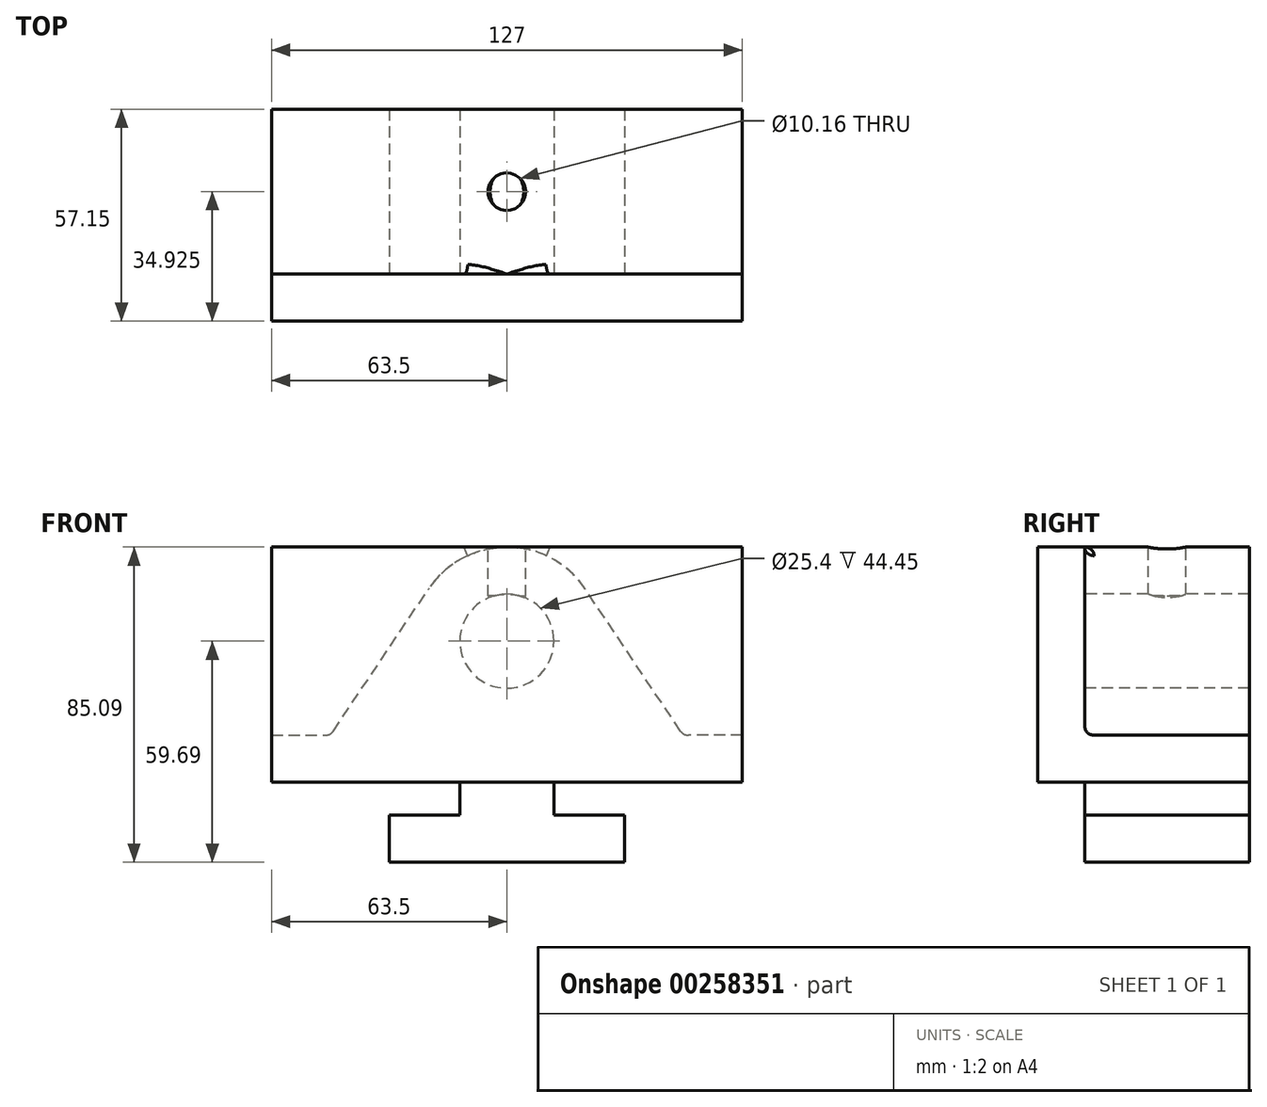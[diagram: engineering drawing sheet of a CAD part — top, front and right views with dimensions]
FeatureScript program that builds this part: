
annotation { "Feature Type Name" : "Feature", "Feature Type Description" : "" }
export const myFeature = defineFeature(function(context is Context, id is Id, definition is map)
    precondition{}
    {
        {
            var Q0;
            Q0=qCreatedBy(makeId("Front.planeOp"),FACE);
            var sketch = newSketch(context, id + "F0", { "sketchPlane" : qUnion([Q0])});
            skLineSegment(sketch, "E0", {"start": v(0, 0) * mm, "end": v(-31.75, 0) * mm});
            skLineSegment(sketch, "E1", {"start": v(0, 0) * mm, "end": v(31.75, 0) * mm});
            skLineSegment(sketch, "E2", {"start": v(31.75, 0) * mm, "end": v(31.75, 12.7) * mm});
            skLineSegment(sketch, "E3", {"start": v(-31.75, 0) * mm, "end": v(-31.75, 12.7) * mm});
            skLineSegment(sketch, "E4", {"start": v(-31.75, 12.7) * mm, "end": v(-12.7, 12.7) * mm});
            skLineSegment(sketch, "E5", {"start": v(31.75, 12.7) * mm, "end": v(12.7, 12.7) * mm});
            skLineSegment(sketch, "E6", {"start": v(12.7, 12.7) * mm, "end": v(12.7, 21.59) * mm});
            skLineSegment(sketch, "E7", {"start": v(-12.7, 12.7) * mm, "end": v(-12.7, 21.59) * mm});
            skLineSegment(sketch, "E8", {"start": v(-12.7, 21.59) * mm, "end": v(-63.5, 21.59) * mm});
            skLineSegment(sketch, "E9", {"start": v(12.7, 21.59) * mm, "end": v(63.5, 21.59) * mm});
            skLineSegment(sketch, "E10", {"start": v(-63.5, 21.59) * mm, "end": v(-63.5, 34.29) * mm});
            skLineSegment(sketch, "E11", {"start": v(63.5, 21.59) * mm, "end": v(63.5, 34.3) * mm});
            skLineSegment(sketch, "E12", {"start": v(63.5, 34.3) * mm, "end": v(47.62, 34.3) * mm});
            skLineSegment(sketch, "E13", {"start": v(-63.5, 34.29) * mm, "end": v(-47.62, 34.29) * mm});
            skLineSegment(sketch, "E14", {"start": v(0, 0) * mm, "end": v(0, 59.7) * mm});
            skCircle(sketch, "E15", {"center": v(0, 59.7) * mm, "radius": 12.7 * mm});
            skLineSegment(sketch, "E16", {"start": v(-47.62, 34.29) * mm, "end": v(-21.1, 73.84) * mm});
            skLineSegment(sketch, "E17", {"start": v(47.62, 34.3) * mm, "end": v(21.1, 73.84) * mm});
            skArc(sketch, "E18", {"start": v(21.1, 73.84) * mm, "mid": v(0, 85.1) * mm, "end": v(-21.1, 73.84) * mm});
            skSolve(sketch);
        }
        {
            var Q0;
            Q0=makeQuery(id+"F0.imprint","IMPRINT",FACE,{"disambiguationData":[TD([[makeQuery(id+"F0.imprint","IMPRINT",EDGE,{"derivedFrom":sQuery(id+"F0.wireOp",EDGE,"E0")}),-1.0]])]});
            extrude(context, id + "F1", {"entities" : qUnion([Q0]), "oppositeDirection" : true, "depth" : 44.45 * mm});
        }
        {
            var Q0;
            Q0=makeQuery(id+"F1.opExtrude","CAP_FACE",FACE,{"disambiguationData":[OSD([sQuery(id+"F0.wireOp",EDGE,"E0"),sQuery(id+"F0.wireOp",EDGE,"E1"),sQuery(id+"F0.wireOp",EDGE,"E2"),sQuery(id+"F0.wireOp",EDGE,"E3"),sQuery(id+"F0.wireOp",EDGE,"E4"),sQuery(id+"F0.wireOp",EDGE,"E5"),sQuery(id+"F0.wireOp",EDGE,"E6"),sQuery(id+"F0.wireOp",EDGE,"E7"),sQuery(id+"F0.wireOp",EDGE,"E8"),sQuery(id+"F0.wireOp",EDGE,"E9"),sQuery(id+"F0.wireOp",EDGE,"E10"),sQuery(id+"F0.wireOp",EDGE,"E11"),sQuery(id+"F0.wireOp",EDGE,"E12"),sQuery(id+"F0.wireOp",EDGE,"E13"),sQuery(id+"F0.wireOp",EDGE,"E15"),sQuery(id+"F0.wireOp",EDGE,"E16"),sQuery(id+"F0.wireOp",EDGE,"E17"),sQuery(id+"F0.wireOp",EDGE,"E18")])],"isStart":true});
            var sketch = newSketch(context, id + "F2", { "sketchPlane" : qUnion([Q0])});
            skPoint(sketch, "E19.oppositeSnap0", {"position": v(0, 85.1) * mm});
            skLineSegment(sketch, "E19.bottom", {"start": v(-63.5, 21.59) * mm, "end": v(63.5, 21.59) * mm});
            skLineSegment(sketch, "E19.top", {"start": v(-63.5, 85.1) * mm, "end": v(63.5, 85.1) * mm});
            skLineSegment(sketch, "E19.left", {"start": v(-63.5, 21.59) * mm, "end": v(-63.5, 85.1) * mm});
            skLineSegment(sketch, "E19.right", {"start": v(63.5, 21.59) * mm, "end": v(63.5, 85.1) * mm});
            skSolve(sketch);
        }
        {
            var Q0;
            {var subQ0=makeQuery(id+"F1.opExtrude","CAP_EDGE",EDGE,{"disambiguationData":[OSD([sQuery(id+"F0.wireOp",EDGE,"E12")])],"isStart":true});Q0=makeQuery(id+"F2.imprint","IMPRINT",FACE,{"disambiguationData":[TD([[makeQuery(id+"F2.imprint","IMPRINT",EDGE,{"derivedFrom":subQ0}),-1.0]])]});}
            var Q1;
            {var subQ5=makeQuery(id+"F1.opExtrude","CAP_EDGE",EDGE,{"disambiguationData":[OSD([sQuery(id+"F0.wireOp",EDGE,"E12")])],"isStart":true});Q1=makeQuery(id+"F2.imprint","IMPRINT",FACE,{"disambiguationData":[TD([[makeQuery(id+"F2.imprint","IMPRINT",EDGE,{"derivedFrom":subQ5}),1.0]])]});}
            var Q2;
            {var subQ6=makeQuery(id+"F1.opExtrude","CAP_EDGE",EDGE,{"disambiguationData":[OSD([sQuery(id+"F0.wireOp",EDGE,"E13")])],"isStart":true});Q2=makeQuery(id+"F2.imprint","IMPRINT",FACE,{"disambiguationData":[TD([[makeQuery(id+"F2.imprint","IMPRINT",EDGE,{"derivedFrom":subQ6}),1.0]])]});}
            var Q3;
            Q3=makeQuery(id+"F2.imprint","IMPRINT",FACE,{"disambiguationData":[TD([[makeQuery(id+"F2.imprint","IMPRINT",EDGE,{"derivedFrom":makeQuery(id+"F1.opExtrude","CAP_EDGE",EDGE,{"disambiguationData":[OSD([sQuery(id+"F0.wireOp",EDGE,"E15")])],"isStart":true})}),1.0]])]});
            extrude(context, id + "F3", {"entities" : qUnion([Q0, Q1, Q2, Q3]), "operationType" : NewBodyOperationType.ADD, "depth" : 12.7 * mm});
        }
        {
            var Q0;
            Q0=makeQuery(id+"F1.opExtrude","SWEPT_EDGE",EDGE,{"disambiguationData":[OSD([sQuery(id+"F0.wireOp",EDGE,"E12"),sQuery(id+"F0.wireOp",EDGE,"E17")])]});
            var Q1;
            Q1=makeQuery(id+"F1.opExtrude","SWEPT_EDGE",EDGE,{"disambiguationData":[OSD([sQuery(id+"F0.wireOp",EDGE,"E13"),sQuery(id+"F0.wireOp",EDGE,"E16")])]});
            var Q2;
            Q2=makeQuery(id+"F1.opExtrude","CAP_EDGE",EDGE,{"disambiguationData":[OSD([sQuery(id+"F0.wireOp",EDGE,"E16")])],"isStart":true});
            var Q3;
            {var subQ1=sQuery(id+"F0.wireOp",EDGE,"E18");Q3=makeQuery(id+"F3.boolean.opBoolean","SPLIT",EDGE,{"disambiguationData":[TD([makeQuery(id+"F1.opExtrude","SWEPT_FACE",FACE,{"disambiguationData":[OSD([sQuery(id+"F0.wireOp",EDGE,"E16")])]})])],"derivedFrom":makeQuery(id+"F1.opExtrude","CAP_EDGE",EDGE,{"disambiguationData":[OSD([subQ1])],"isStart":true})});}
            var Q4;
            {var subQ0=sQuery(id+"F0.wireOp",EDGE,"E18");Q4=makeQuery(id+"F3.boolean.opBoolean","SPLIT",EDGE,{"disambiguationData":[TD([makeQuery(id+"F1.opExtrude","SWEPT_FACE",FACE,{"disambiguationData":[OSD([sQuery(id+"F0.wireOp",EDGE,"E17")])]})])],"derivedFrom":makeQuery(id+"F1.opExtrude","CAP_EDGE",EDGE,{"disambiguationData":[OSD([subQ0])],"isStart":true})});}
            var Q5;
            Q5=makeQuery(id+"F1.opExtrude","CAP_EDGE",EDGE,{"disambiguationData":[OSD([sQuery(id+"F0.wireOp",EDGE,"E17")])],"isStart":true});
            var Q6;
            Q6=makeQuery(id+"F1.opExtrude","CAP_EDGE",EDGE,{"disambiguationData":[OSD([sQuery(id+"F0.wireOp",EDGE,"E12")])],"isStart":true});
            var Q7;
            Q7=makeQuery(id+"F1.opExtrude","CAP_EDGE",EDGE,{"disambiguationData":[OSD([sQuery(id+"F0.wireOp",EDGE,"E13")])],"isStart":true});
            fillet(context, id + "F4", {"entities" : qUnion([Q0, Q1, Q2, Q3, Q4, Q5, Q6, Q7]), "radius" : 2.54 * mm, "tangentPropagation" : true, "allowEdgeOverflow" : false});
        }
        {
            var Q0;
            Q0=makeQuery(id+"F3.opExtrude","SWEPT_FACE",FACE,{"disambiguationData":[OSD([sQuery(id+"F2.wireOp",EDGE,"E19.top")])]});
            var sketch = newSketch(context, id + "F5", { "sketchPlane" : qUnion([Q0])});
            skLineSegment(sketch, "E20", {"start": v(0, 0) * mm, "end": v(0, 22.23) * mm});
            skSolve(sketch);
        }
        {
            var Q0;
            Q0=sQuery(id+"F5.wireOp",VERTEX,"E20.end");
            var Q1;
            Q1=makeQuery(id+"F1.opExtrude","SWEPT_BODY",BODY,{"disambiguationData":[OSD([sQuery(id+"F0.wireOp",EDGE,"E0"),sQuery(id+"F0.wireOp",EDGE,"E1"),sQuery(id+"F0.wireOp",EDGE,"E2"),sQuery(id+"F0.wireOp",EDGE,"E3"),sQuery(id+"F0.wireOp",EDGE,"E4"),sQuery(id+"F0.wireOp",EDGE,"E5"),sQuery(id+"F0.wireOp",EDGE,"E6"),sQuery(id+"F0.wireOp",EDGE,"E7"),sQuery(id+"F0.wireOp",EDGE,"E8"),sQuery(id+"F0.wireOp",EDGE,"E9"),sQuery(id+"F0.wireOp",EDGE,"E10"),sQuery(id+"F0.wireOp",EDGE,"E11"),sQuery(id+"F0.wireOp",EDGE,"E12"),sQuery(id+"F0.wireOp",EDGE,"E13"),sQuery(id+"F0.wireOp",EDGE,"E15"),sQuery(id+"F0.wireOp",EDGE,"E16"),sQuery(id+"F0.wireOp",EDGE,"E17"),sQuery(id+"F0.wireOp",EDGE,"E18")])]});
            hole(context, id + "F6", {"style" : HoleStyle.SIMPLE, "endStyle" : HoleEndStyle.BLIND, "holeDiameter" : 10.16 * mm, "holeDepth" : 12.7 * mm, "tappedDepth" : 12.7 * mm, "tapClearance" : 3, "locations" : qUnion([Q0]), "scope" : qUnion([Q1])});
        }
    });
